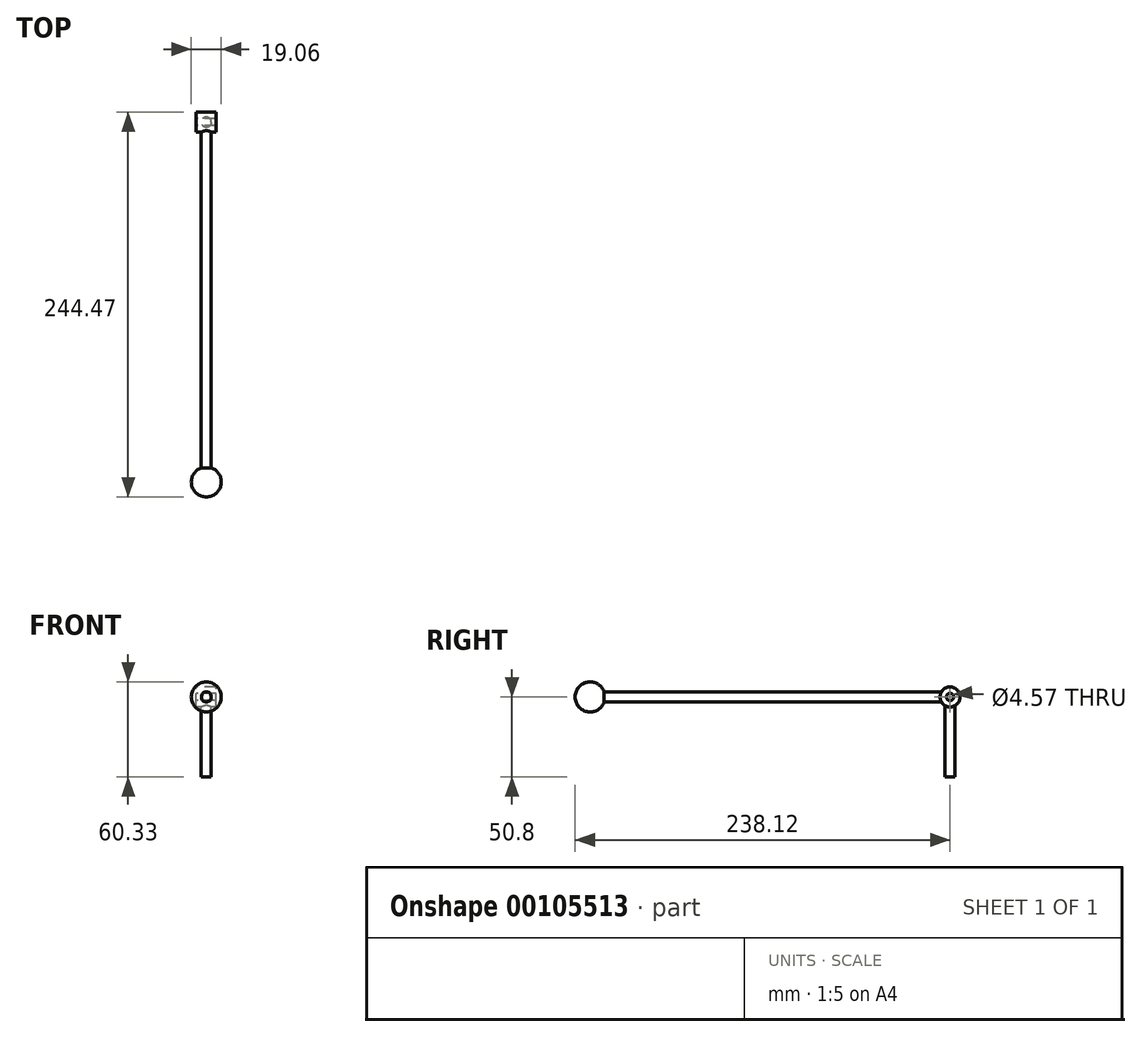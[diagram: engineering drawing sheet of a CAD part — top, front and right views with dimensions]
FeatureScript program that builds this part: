
annotation { "Feature Type Name" : "Feature", "Feature Type Description" : "" }
export const myFeature = defineFeature(function(context is Context, id is Id, definition is map)
    precondition{}
    {
        {
            var Q0;
            Q0=qCreatedBy(makeId("Front.planeOp"),FACE);
            var sketch = newSketch(context, id + "F0", { "sketchPlane" : qUnion([Q0])});
            skCircle(sketch, "E0", {"center": v(0, 0) * mm, "radius": 3.18 * mm});
            skSolve(sketch);
        }
        {
            var Q0;
            Q0=makeQuery(id+"F0.imprint","IMPRINT",FACE,{"disambiguationData":[TD([[makeQuery(id+"F0.imprint","IMPRINT",EDGE,{"derivedFrom":sQuery(id+"F0.wireOp",EDGE,"E0")}),1.0]])]});
            extrude(context, id + "F1", {"entities" : qUnion([Q0]), "depth" : 228.6 * mm});
        }
        {
            var Q0;
            Q0=qCreatedBy(makeId("Top.planeOp"),FACE);
            var sketch = newSketch(context, id + "F2", { "sketchPlane" : qUnion([Q0])});
            skCircle(sketch, "E1", {"center": v(0, 0) * mm, "radius": 3.18 * mm});
            skSolve(sketch);
        }
        {
            var Q0;
            Q0=makeQuery(id+"F2.imprint","IMPRINT",FACE,{"disambiguationData":[TD([[makeQuery(id+"F2.imprint","IMPRINT",EDGE,{"derivedFrom":sQuery(id+"F2.wireOp",EDGE,"E1")}),1.0]])]});
            extrude(context, id + "F3", {"entities" : qUnion([Q0]), "operationType" : NewBodyOperationType.ADD, "oppositeDirection" : true, "depth" : 50.8 * mm});
        }
        {
            var Q0;
            Q0=qCreatedBy(makeId("Right.planeOp"),FACE);
            var sketch = newSketch(context, id + "F4", { "sketchPlane" : qUnion([Q0])});
            skCircle(sketch, "E2", {"center": v(0, 0) * mm, "radius": 6.35 * mm});
            skSolve(sketch);
        }
        {
            var Q0;
            Q0=makeQuery(id+"F4.imprint","IMPRINT",FACE,{"disambiguationData":[TD([[makeQuery(id+"F4.imprint","IMPRINT",EDGE,{"derivedFrom":sQuery(id+"F4.wireOp",EDGE,"E2")}),1.0]])]});
            extrude(context, id + "F5", {"entities" : qUnion([Q0]), "operationType" : NewBodyOperationType.ADD, "endBound" : BoundingType.SYMMETRIC, "depth" : 12.7 * mm});
        }
        {
            var Q0;
            Q0=qCreatedBy(makeId("Right.planeOp"),FACE);
            var sketch = newSketch(context, id + "F6", { "sketchPlane" : qUnion([Q0])});
            skLineSegment(sketch, "E3.0", {"start": v(-228.6, -3.18) * mm, "end": v(-228.6, 3.18) * mm, "construction": true});
            skArc(sketch, "E4", {"start": v(-228.6, -9.53) * mm, "mid": v(-219.08, 0) * mm, "end": v(-228.6, 9.53) * mm});
            skLineSegment(sketch, "E5", {"start": v(-228.6, 9.53) * mm, "end": v(-228.6, -9.53) * mm});
            skPoint(sketch, "E6.orphan", {"position": v(-228.6, 12.1) * mm});
            skSolve(sketch);
        }
        {
            var Q0;
            Q0=makeQuery(id+"F6.imprint","IMPRINT",FACE,{"disambiguationData":[TD([[makeQuery(id+"F6.imprint","IMPRINT",EDGE,{"derivedFrom":sQuery(id+"F6.wireOp",EDGE,"E4")}),1.0]])]});
            var Q1;
            Q1=sQuery(id+"F6.wireOp",EDGE,"E5");
            revolve(context, id + "F7", {"operationType" : NewBodyOperationType.ADD, "entities" : qUnion([Q0]), "axis" : qUnion([Q1]), "revolveType" : RevolveType.FULL});
        }
        {
            var Q0;
            Q0=makeQuery(id+"F5.opExtrude","CAP_FACE",FACE,{"disambiguationData":[OSD([sQuery(id+"F4.wireOp",EDGE,"E2")])],"isStart":false});
            var sketch = newSketch(context, id + "F8", { "sketchPlane" : qUnion([Q0])});
            skCircle(sketch, "E7", {"center": v(0, 0) * mm, "radius": 2.29 * mm});
            skSolve(sketch);
        }
        {
            var Q0;
            Q0=makeQuery(id+"F8.imprint","IMPRINT",FACE,{"disambiguationData":[TD([[makeQuery(id+"F8.imprint","IMPRINT",EDGE,{"derivedFrom":sQuery(id+"F8.wireOp",EDGE,"E7")}),1.0]])]});
            extrude(context, id + "F9", {"entities" : qUnion([Q0]), "operationType" : NewBodyOperationType.REMOVE, "endBound" : BoundingType.SYMMETRIC, "depth" : 127 * mm});
        }
    });
